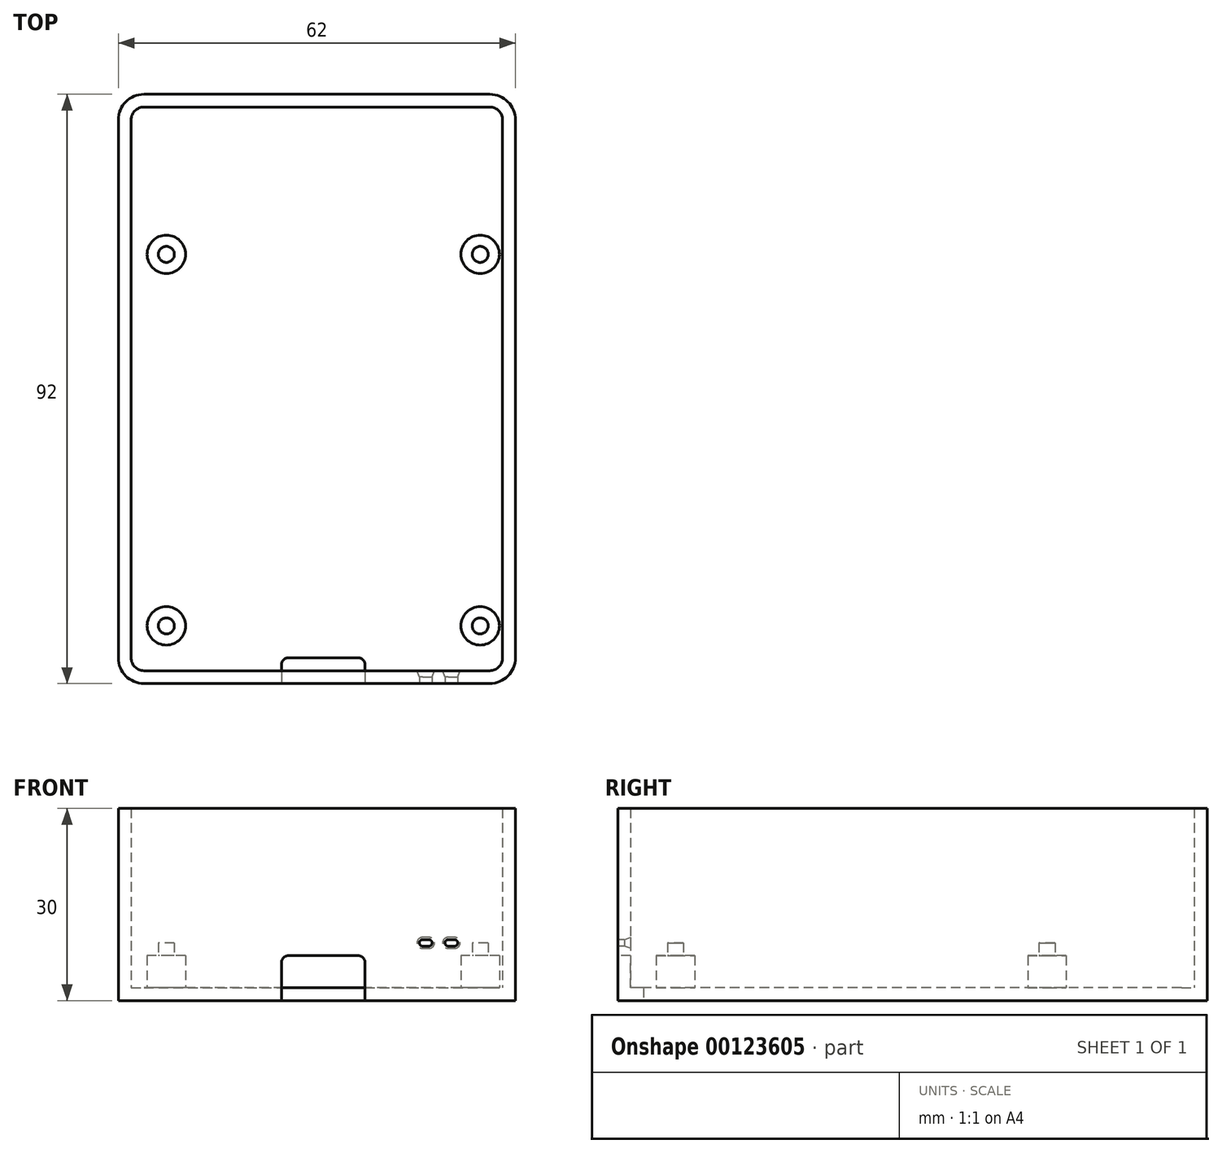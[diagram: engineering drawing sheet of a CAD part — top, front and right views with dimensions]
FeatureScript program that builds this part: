
annotation { "Feature Type Name" : "Feature", "Feature Type Description" : "" }
export const myFeature = defineFeature(function(context is Context, id is Id, definition is map)
    precondition{}
    {
        {
            var Q0;
            Q0=qCreatedBy(makeId("Top.planeOp"),FACE);
            var sketch = newSketch(context, id + "F0", { "sketchPlane" : qUnion([Q0])});
            skLineSegment(sketch, "E0.bottom", {"start": v(62, 0) * mm, "end": v(0, 0) * mm});
            skLineSegment(sketch, "E0.top", {"start": v(62, 92) * mm, "end": v(0, 92) * mm});
            skLineSegment(sketch, "E0.left", {"start": v(62, 0) * mm, "end": v(62, 92) * mm});
            skLineSegment(sketch, "E0.right", {"start": v(0, 0) * mm, "end": v(0, 92) * mm});
            skSolve(sketch);
        }
        {
            var Q0;
            Q0=makeQuery(id+"F0.imprint","IMPRINT",FACE,{"disambiguationData":[TD([[makeQuery(id+"F0.imprint","IMPRINT",EDGE,{"derivedFrom":sQuery(id+"F0.wireOp",EDGE,"E0.bottom")}),-1.0]])]});
            extrude(context, id + "F1", {"entities" : qUnion([Q0]), "depth" : 2 * mm});
        }
        {
            var Q0;
            Q0=makeQuery(id+"F1.opExtrude","CAP_FACE",FACE,{"disambiguationData":[OSD([sQuery(id+"F0.wireOp",EDGE,"E0.bottom"),sQuery(id+"F0.wireOp",EDGE,"E0.top"),sQuery(id+"F0.wireOp",EDGE,"E0.left"),sQuery(id+"F0.wireOp",EDGE,"E0.right")])],"isStart":false});
            var sketch = newSketch(context, id + "F2", { "sketchPlane" : qUnion([Q0])});
            skLineSegment(sketch, "E1.0", {"start": v(2, 2) * mm, "end": v(60, 2) * mm});
            skLineSegment(sketch, "E1.1", {"start": v(2, 90) * mm, "end": v(2, 2) * mm});
            skLineSegment(sketch, "E1.2", {"start": v(60, 90) * mm, "end": v(2, 90) * mm});
            skLineSegment(sketch, "E1.3", {"start": v(60, 2) * mm, "end": v(60, 90) * mm});
            skLineSegment(sketch, "E2.bottom", {"start": v(7.5, 67) * mm, "end": v(56.5, 67) * mm, "construction": true});
            skLineSegment(sketch, "E2.top", {"start": v(7.5, 9) * mm, "end": v(56.5, 9) * mm, "construction": true});
            skLineSegment(sketch, "E2.left", {"start": v(7.5, 67) * mm, "end": v(7.5, 9) * mm, "construction": true});
            skLineSegment(sketch, "E2.right", {"start": v(56.5, 67) * mm, "end": v(56.5, 9) * mm, "construction": true});
            skCircle(sketch, "E3", {"center": v(7.5, 67) * mm, "radius": 3 * mm});
            skCircle(sketch, "E4", {"center": v(56.5, 67) * mm, "radius": 3 * mm});
            skCircle(sketch, "E5", {"center": v(56.5, 9) * mm, "radius": 3 * mm});
            skCircle(sketch, "E6", {"center": v(7.5, 9) * mm, "radius": 3 * mm});
            skSolve(sketch);
        }
        {
            var Q0;
            Q0=makeQuery(id+"F2.imprint","IMPRINT",FACE,{"disambiguationData":[TD([[makeQuery(id+"F2.imprint","IMPRINT",EDGE,{"derivedFrom":sQuery(id+"F2.wireOp",EDGE,"E1.0")}),-1.0]])]});
            var Q1;
            Q1=makeQuery(id+"F2.imprint","IMPRINT",FACE,{"disambiguationData":[TD([[makeQuery(id+"F2.imprint","IMPRINT",EDGE,{"derivedFrom":sQuery(id+"F2.wireOp",EDGE,"E3")}),1.0]])]});
            var Q2;
            Q2=makeQuery(id+"F2.imprint","IMPRINT",FACE,{"disambiguationData":[TD([[makeQuery(id+"F2.imprint","IMPRINT",EDGE,{"derivedFrom":sQuery(id+"F2.wireOp",EDGE,"E4")}),1.0]])]});
            var Q3;
            Q3=makeQuery(id+"F2.imprint","IMPRINT",FACE,{"disambiguationData":[TD([[makeQuery(id+"F2.imprint","IMPRINT",EDGE,{"derivedFrom":sQuery(id+"F2.wireOp",EDGE,"E6")}),1.0]])]});
            var Q4;
            Q4=makeQuery(id+"F2.imprint","IMPRINT",FACE,{"disambiguationData":[TD([[makeQuery(id+"F2.imprint","IMPRINT",EDGE,{"derivedFrom":sQuery(id+"F2.wireOp",EDGE,"E5")}),1.0]])]});
            extrude(context, id + "F3", {"entities" : qUnion([Q0, Q1, Q2, Q3, Q4]), "operationType" : NewBodyOperationType.ADD, "depth" : 28 * mm});
        }
        {
            var Q0;
            Q0=makeQuery(id+"F3.opExtrude","CAP_FACE",FACE,{"disambiguationData":[OSD([sQuery(id+"F2.wireOp",EDGE,"E3")])],"isStart":false});
            var Q1;
            Q1=makeQuery(id+"F3.opExtrude","CAP_FACE",FACE,{"disambiguationData":[OSD([sQuery(id+"F2.wireOp",EDGE,"E4")])],"isStart":false});
            var Q2;
            Q2=makeQuery(id+"F3.opExtrude","CAP_FACE",FACE,{"disambiguationData":[OSD([sQuery(id+"F2.wireOp",EDGE,"E5")])],"isStart":false});
            var Q3;
            Q3=makeQuery(id+"F3.opExtrude","CAP_FACE",FACE,{"disambiguationData":[OSD([sQuery(id+"F2.wireOp",EDGE,"E6")])],"isStart":false});
            extrude(context, id + "F4", {"entities" : qUnion([Q0, Q1, Q2, Q3]), "operationType" : NewBodyOperationType.REMOVE, "oppositeDirection" : true, "depth" : 23 * mm});
        }
        {
            var Q0;
            Q0=makeQuery(id+"F4.boolean.opBoolean","COPY",FACE,{"derivedFrom":makeQuery(id+"F4.opExtrude","CAP_FACE",FACE,{"disambiguationData":[OSD([sQuery(id+"F2.wireOp",EDGE,"E6")])],"isStart":false})});
            var sketch = newSketch(context, id + "F5", { "sketchPlane" : qUnion([Q0])});
            skCircle(sketch, "E7", {"center": v(7.5, 9) * mm, "radius": 1.25 * mm});
            skSolve(sketch);
        }
        {
            var Q0;
            Q0=qSketchRegion(id+"F5",true);
            extrude(context, id + "F6", {"entities" : qUnion([Q0]), "operationType" : NewBodyOperationType.ADD, "depth" : 2 * mm});
        }
        {
            var Q0;
            Q0=makeQuery(id+"F4.boolean.opBoolean","COPY",FACE,{"derivedFrom":makeQuery(id+"F4.opExtrude","CAP_FACE",FACE,{"disambiguationData":[OSD([sQuery(id+"F2.wireOp",EDGE,"E5")])],"isStart":false})});
            var sketch = newSketch(context, id + "F7", { "sketchPlane" : qUnion([Q0])});
            skCircle(sketch, "E8", {"center": v(56.5, 9) * mm, "radius": 1.25 * mm});
            skSolve(sketch);
        }
        {
            var Q0;
            Q0=qSketchRegion(id+"F7",true);
            extrude(context, id + "F8", {"entities" : qUnion([Q0]), "operationType" : NewBodyOperationType.ADD, "depth" : 2 * mm});
        }
        {
            var Q0;
            Q0=makeQuery(id+"F4.boolean.opBoolean","COPY",FACE,{"derivedFrom":makeQuery(id+"F4.opExtrude","CAP_FACE",FACE,{"disambiguationData":[OSD([sQuery(id+"F2.wireOp",EDGE,"E4")])],"isStart":false})});
            var sketch = newSketch(context, id + "F9", { "sketchPlane" : qUnion([Q0])});
            skCircle(sketch, "E9", {"center": v(56.5, 67) * mm, "radius": 1.25 * mm});
            skSolve(sketch);
        }
        {
            var Q0;
            Q0=qSketchRegion(id+"F9",true);
            extrude(context, id + "F10", {"entities" : qUnion([Q0]), "operationType" : NewBodyOperationType.ADD, "depth" : 2 * mm});
        }
        {
            var Q0;
            Q0=makeQuery(id+"F4.boolean.opBoolean","COPY",FACE,{"derivedFrom":makeQuery(id+"F4.opExtrude","CAP_FACE",FACE,{"disambiguationData":[OSD([sQuery(id+"F2.wireOp",EDGE,"E3")])],"isStart":false})});
            var sketch = newSketch(context, id + "F11", { "sketchPlane" : qUnion([Q0])});
            skCircle(sketch, "E10", {"center": v(7.5, 67) * mm, "radius": 1.25 * mm});
            skSolve(sketch);
        }
        {
            var Q0;
            Q0=qSketchRegion(id+"F11",true);
            extrude(context, id + "F12", {"entities" : qUnion([Q0]), "operationType" : NewBodyOperationType.ADD, "depth" : 2 * mm});
        }
        {
            var Q0;
            {var subQ0=sQuery(id+"F0.wireOp",EDGE,"E0.bottom");Q0=makeQuery(id+"F3.boolean.opBoolean","MERGE",FACE,{"derivedFrom":[makeQuery(id+"F1.opExtrude","SWEPT_FACE",FACE,{"disambiguationData":[OSD([subQ0])]}),makeQuery(id+"F3.opExtrude","SWEPT_FACE",FACE,{"disambiguationData":[OSD([subQ0])]})]});}
            var sketch = newSketch(context, id + "F13", { "sketchPlane" : qUnion([Q0])});
            skLineSegment(sketch, "E11.bottom", {"start": v(51.5, 9.5) * mm, "end": v(52.5, 9.5) * mm});
            skLineSegment(sketch, "E11.top", {"start": v(51.5, 8.5) * mm, "end": v(52.5, 8.5) * mm});
            skLineSegment(sketch, "E11.left", {"start": v(51, 9) * mm, "end": v(51, 9) * mm});
            skLineSegment(sketch, "E11.right", {"start": v(53, 9) * mm, "end": v(53, 9) * mm});
            skLineSegment(sketch, "E12.bottom", {"start": v(47.5, 9.5) * mm, "end": v(48.5, 9.5) * mm});
            skLineSegment(sketch, "E12.top", {"start": v(47.5, 8.5) * mm, "end": v(48.5, 8.5) * mm});
            skLineSegment(sketch, "E12.left", {"start": v(47, 9) * mm, "end": v(47, 9) * mm});
            skLineSegment(sketch, "E12.right", {"start": v(49, 9) * mm, "end": v(49, 9) * mm});
            skLineSegment(sketch, "E13", {"start": v(56.5, 9.01) * mm, "end": v(56.5, 6.99) * mm, "construction": true});
            skLineSegment(sketch, "E14", {"start": v(52.63, 7) * mm, "end": v(33.92, 7) * mm, "construction": true});
            skLineSegment(sketch, "E15.bottom", {"start": v(37.5, 7) * mm, "end": v(26.5, 7) * mm});
            skLineSegment(sketch, "E15.top", {"start": v(38.5, 0) * mm, "end": v(25.5, 0) * mm});
            skLineSegment(sketch, "E15.left", {"start": v(38.5, 6) * mm, "end": v(38.5, 0) * mm});
            skLineSegment(sketch, "E15.right", {"start": v(25.5, 6) * mm, "end": v(25.5, 0) * mm});
            skPoint(sketch, "E16.visualSharp", {"position": v(25.5, 7) * mm});
            skArc(sketch, "E16.filletArc", {"start": v(26.5, 7) * mm, "mid": v(25.8, 6.7) * mm, "end": v(25.5, 6) * mm});
            skPoint(sketch, "E17.visualSharp", {"position": v(38.5, 7) * mm});
            skArc(sketch, "E17.filletArc", {"start": v(38.5, 6) * mm, "mid": v(38.2, 6.7) * mm, "end": v(37.5, 7) * mm});
            skPoint(sketch, "E18.visualSharp", {"position": v(47, 9.5) * mm});
            skArc(sketch, "E18.filletArc", {"start": v(47.5, 9.5) * mm, "mid": v(47.15, 9.35) * mm, "end": v(47, 9) * mm});
            skPoint(sketch, "E19.visualSharp", {"position": v(49, 9.5) * mm});
            skArc(sketch, "E19.filletArc", {"start": v(49, 9) * mm, "mid": v(48.85, 9.35) * mm, "end": v(48.5, 9.5) * mm});
            skPoint(sketch, "E20.visualSharp", {"position": v(49, 8.5) * mm});
            skArc(sketch, "E20.filletArc", {"start": v(48.5, 8.5) * mm, "mid": v(48.85, 8.65) * mm, "end": v(49, 9) * mm});
            skPoint(sketch, "E21.visualSharp", {"position": v(47, 8.5) * mm});
            skArc(sketch, "E21.filletArc", {"start": v(47, 9) * mm, "mid": v(47.15, 8.65) * mm, "end": v(47.5, 8.5) * mm});
            skPoint(sketch, "E22.visualSharp", {"position": v(51, 9.5) * mm});
            skArc(sketch, "E22.filletArc", {"start": v(51.5, 9.5) * mm, "mid": v(51.15, 9.35) * mm, "end": v(51, 9) * mm});
            skPoint(sketch, "E23.visualSharp", {"position": v(53, 9.5) * mm});
            skArc(sketch, "E23.filletArc", {"start": v(53, 9) * mm, "mid": v(52.85, 9.35) * mm, "end": v(52.5, 9.5) * mm});
            skPoint(sketch, "E24.visualSharp", {"position": v(53, 8.5) * mm});
            skArc(sketch, "E24.filletArc", {"start": v(52.5, 8.5) * mm, "mid": v(52.85, 8.65) * mm, "end": v(53, 9) * mm});
            skPoint(sketch, "E25.visualSharp", {"position": v(51, 8.5) * mm});
            skArc(sketch, "E25.filletArc", {"start": v(51, 9) * mm, "mid": v(51.15, 8.65) * mm, "end": v(51.5, 8.5) * mm});
            skSolve(sketch);
        }
        {
            var Q0;
            Q0=makeQuery(id+"F13.imprint","IMPRINT",FACE,{"disambiguationData":[TD([[makeQuery(id+"F13.imprint","IMPRINT",EDGE,{"derivedFrom":sQuery(id+"F13.wireOp",EDGE,"E15.bottom")}),1.0]])]});
            var Q1;
            Q1=makeQuery(id+"F13.imprint","IMPRINT",FACE,{"disambiguationData":[TD([[makeQuery(id+"F13.imprint","IMPRINT",EDGE,{"derivedFrom":sQuery(id+"F13.wireOp",EDGE,"E12.bottom")}),-1.0]])]});
            var Q2;
            Q2=makeQuery(id+"F13.imprint","IMPRINT",FACE,{"disambiguationData":[TD([[makeQuery(id+"F13.imprint","IMPRINT",EDGE,{"derivedFrom":sQuery(id+"F13.wireOp",EDGE,"E11.bottom")}),-1.0]])]});
            extrude(context, id + "F14", {"entities" : qUnion([Q0, Q1, Q2]), "operationType" : NewBodyOperationType.REMOVE, "oppositeDirection" : true, "depth" : 4 * mm});
        }
        {
            var Q0;
            Q0=makeQuery(id+"F14.boolean.opBoolean","COPY",EDGE,{"derivedFrom":makeQuery(id+"F14.opExtrude","CAP_EDGE",EDGE,{"disambiguationData":[OSD([sQuery(id+"F13.wireOp",EDGE,"E15.right")])],"isStart":false})});
            var Q1;
            Q1=makeQuery(id+"F14.boolean.opBoolean","COPY",EDGE,{"derivedFrom":makeQuery(id+"F14.opExtrude","CAP_EDGE",EDGE,{"disambiguationData":[OSD([sQuery(id+"F13.wireOp",EDGE,"E15.left")])],"isStart":false})});
            fillet(context, id + "F15", {"entities" : qUnion([Q0, Q1]), "radius" : 1 * mm, "tangentPropagation" : true, "allowEdgeOverflow" : false});
        }
        {
            var Q0;
            Q0=makeQuery(id+"F3.opExtrude","SWEPT_EDGE",EDGE,{"disambiguationData":[OSD([sQuery(id+"F2.wireOp",EDGE,"E1.1"),sQuery(id+"F2.wireOp",EDGE,"E1.2")])]});
            var Q1;
            Q1=makeQuery(id+"F3.opExtrude","SWEPT_EDGE",EDGE,{"disambiguationData":[OSD([sQuery(id+"F2.wireOp",EDGE,"E1.2"),sQuery(id+"F2.wireOp",EDGE,"E1.3")])]});
            var Q2;
            Q2=makeQuery(id+"F3.opExtrude","SWEPT_EDGE",EDGE,{"disambiguationData":[OSD([sQuery(id+"F2.wireOp",EDGE,"E1.0"),sQuery(id+"F2.wireOp",EDGE,"E1.3")])]});
            var Q3;
            Q3=makeQuery(id+"F3.opExtrude","SWEPT_EDGE",EDGE,{"disambiguationData":[OSD([sQuery(id+"F2.wireOp",EDGE,"E1.0"),sQuery(id+"F2.wireOp",EDGE,"E1.1")])]});
            fillet(context, id + "F16", {"entities" : qUnion([Q0, Q1, Q2, Q3]), "radius" : 2 * mm, "tangentPropagation" : true, "allowEdgeOverflow" : false});
        }
        {
            var Q0;
            {var subQ0=sQuery(id+"F0.wireOp",EDGE,"E0.right");var subQ1=sQuery(id+"F0.wireOp",EDGE,"E0.top");Q0=makeQuery(id+"F3.boolean.opBoolean","MERGE",EDGE,{"derivedFrom":[makeQuery(id+"F1.opExtrude","SWEPT_EDGE",EDGE,{"disambiguationData":[OSD([subQ1,subQ0])]}),makeQuery(id+"F3.opExtrude","SWEPT_EDGE",EDGE,{"disambiguationData":[OSD([subQ1,subQ0])]})]});}
            var Q1;
            {var subQ0=sQuery(id+"F0.wireOp",EDGE,"E0.left");var subQ1=sQuery(id+"F0.wireOp",EDGE,"E0.top");Q1=makeQuery(id+"F3.boolean.opBoolean","MERGE",EDGE,{"derivedFrom":[makeQuery(id+"F1.opExtrude","SWEPT_EDGE",EDGE,{"disambiguationData":[OSD([subQ1,subQ0])]}),makeQuery(id+"F3.opExtrude","SWEPT_EDGE",EDGE,{"disambiguationData":[OSD([subQ1,subQ0])]})]});}
            var Q2;
            {var subQ0=sQuery(id+"F0.wireOp",EDGE,"E0.left");var subQ1=sQuery(id+"F0.wireOp",EDGE,"E0.bottom");Q2=makeQuery(id+"F3.boolean.opBoolean","MERGE",EDGE,{"derivedFrom":[makeQuery(id+"F1.opExtrude","SWEPT_EDGE",EDGE,{"disambiguationData":[OSD([subQ1,subQ0])]}),makeQuery(id+"F3.opExtrude","SWEPT_EDGE",EDGE,{"disambiguationData":[OSD([subQ1,subQ0])]})]});}
            var Q3;
            {var subQ0=sQuery(id+"F0.wireOp",EDGE,"E0.right");var subQ1=sQuery(id+"F0.wireOp",EDGE,"E0.bottom");Q3=makeQuery(id+"F3.boolean.opBoolean","MERGE",EDGE,{"derivedFrom":[makeQuery(id+"F1.opExtrude","SWEPT_EDGE",EDGE,{"disambiguationData":[OSD([subQ1,subQ0])]}),makeQuery(id+"F3.opExtrude","SWEPT_EDGE",EDGE,{"disambiguationData":[OSD([subQ1,subQ0])]})]});}
            fillet(context, id + "F17", {"entities" : qUnion([Q0, Q1, Q2, Q3]), "radius" : 4 * mm, "tangentPropagation" : true, "allowEdgeOverflow" : false});
        }
        {
            var Q0;
            Q0=makeQuery(id+"F14.boolean.opBoolean","INTERSECT",EDGE,{"derivedFrom":[makeQuery(id+"F3.opExtrude","SWEPT_FACE",FACE,{"disambiguationData":[OSD([sQuery(id+"F2.wireOp",EDGE,"E1.0")])]}),makeQuery(id+"F14.opExtrude","SWEPT_FACE",FACE,{"disambiguationData":[OSD([sQuery(id+"F13.wireOp",EDGE,"E22.filletArc"),sQuery(id+"F13.wireOp",EDGE,"E25.filletArc")])]})]});
            var Q1;
            Q1=makeQuery(id+"F14.boolean.opBoolean","INTERSECT",EDGE,{"derivedFrom":[makeQuery(id+"F3.opExtrude","SWEPT_FACE",FACE,{"disambiguationData":[OSD([sQuery(id+"F2.wireOp",EDGE,"E1.0")])]}),makeQuery(id+"F14.opExtrude","SWEPT_FACE",FACE,{"disambiguationData":[OSD([sQuery(id+"F13.wireOp",EDGE,"E18.filletArc"),sQuery(id+"F13.wireOp",EDGE,"E21.filletArc")])]})]});
            chamfer(context, id + "F18", {"entities" : qUnion([Q0, Q1]), "chamferType" : ChamferType.OFFSET_ANGLE, "width" : 1 * mm, "oppositeDirection" : false, "angle" : 20 * degree, "tangentPropagation" : true});
        }
    });
